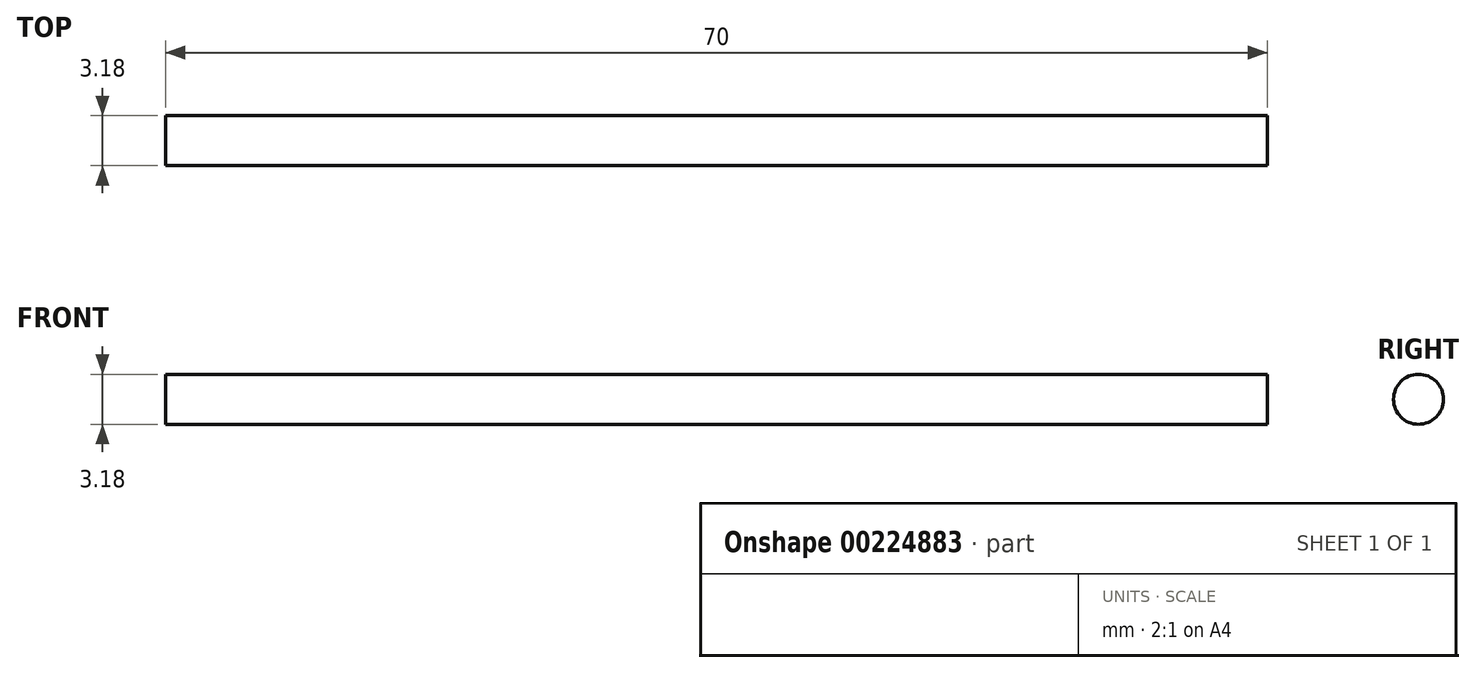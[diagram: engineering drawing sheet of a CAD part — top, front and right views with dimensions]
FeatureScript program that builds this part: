
annotation { "Feature Type Name" : "Feature", "Feature Type Description" : "" }
export const myFeature = defineFeature(function(context is Context, id is Id, definition is map)
    precondition{}
    {
        {
            var Q0;
            Q0=qCreatedBy(makeId("Right.planeOp"),FACE);
            var sketch = newSketch(context, id + "F0", { "sketchPlane" : qUnion([Q0])});
            skCircle(sketch, "E0", {"center": v(0, 0) * mm, "radius": 1.59 * mm});
            skSolve(sketch);
        }
        {
            var Q0;
            Q0 = qSketchRegion(id + "F0", true);
            extrude(context, id + "F1", {"entities" : qUnion([Q0]), "depth" : 70 * mm});
        }
    });
